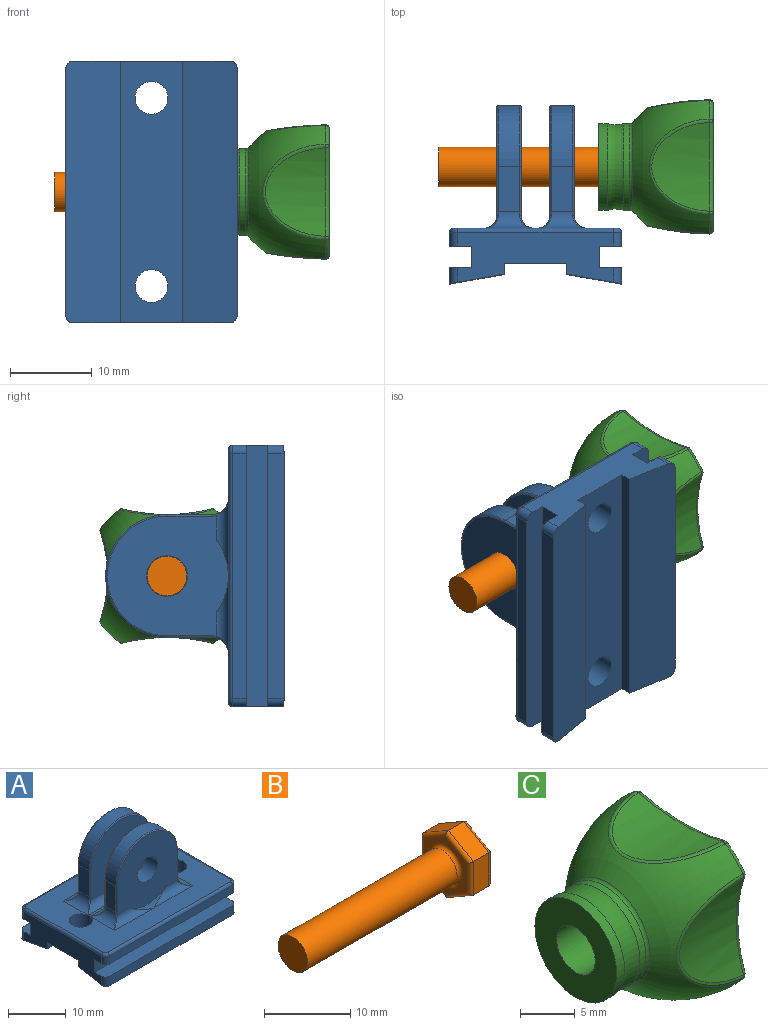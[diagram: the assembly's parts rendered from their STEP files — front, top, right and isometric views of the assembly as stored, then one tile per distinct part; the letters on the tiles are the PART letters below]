
ASSEMBLY  parts=3 mates=4
PART A: 92 faces, bbox 32.2x21.2x22.5 mm
  f0: cylinder r=1.5mm len=9.5mm, axis (1,0,0), area 13.6mm2, adj f11,f23,f50,f75
  f1: cylinder r=1.5mm len=9.5mm, axis (1,0,0), area 13.6mm2, adj f11,f23,f44,f75
  f2: cylinder r=1.5mm len=9.5mm, axis (1,0,0), area 13.6mm2, adj f19,f23,f57,f74
  f3: cylinder r=1.5mm len=9.5mm, axis (1,0,0), area 13.6mm2, adj f19,f23,f51,f74
  f4: cylinder r=1.5mm len=9.5mm, axis (-1,0,0), area 13.6mm2, adj f13,f23,f65,f73
  f5: cylinder r=1.5mm len=9.5mm, axis (-1,0,0), area 13.6mm2, adj f13,f23,f71,f73
  f6: cylinder r=1.5mm len=9.5mm, axis (-1,0,0), area 13.6mm2, adj f18,f23,f58,f72
  f7: cylinder r=1.5mm len=9.5mm, axis (-1,0,0), area 13.6mm2, adj f18,f23,f64,f72
  f8: plane 5.5x2.6mm, normal (-1,0,0), area 14.3mm2, adj f9,f39,f46,f67
  f9: cylinder r=7.5mm len=15mm, axis (0,1,0), area 61.3mm2, adj f8,f10,f47,f68
  f10: plane 5.5x2.6mm, normal (1,0,0), area 14.3mm2, adj f9,f38,f48,f69
  f11: plane 14.8x14.72mm, normal (0,1,0), area 160.9mm2, adj f0,f1,f12,f45,f46,f47,f48,f49
  f12: cylinder r=2.5mm len=5mm, axis (0,1,0), area 47.1mm2, adj f11,f13
  f13: plane 14.8x14.72mm, normal (0,-1,0), area 160.9mm2, adj f4,f5,f12,f66,f67,f68,f69,f70
  f14: plane 5.5x2.6mm, normal (1,0,0), area 14.3mm2, adj f15,f41,f55,f62
  f15: cylinder r=7.5mm len=15mm, axis (0,1,0), area 61.3mm2, adj f14,f16,f54,f61
  f16: plane 5.5x2.6mm, normal (-1,0,0), area 14.3mm2, adj f15,f40,f53,f60
  f17: cylinder r=2.5mm len=5mm, axis (0,1,0), area 47.1mm2, adj f18,f19
  f18: plane 14.8x14.72mm, normal (0,-1,0), area 160.9mm2, adj f6,f7,f17,f59,f60,f61,f62,f63
  f19: plane 14.8x14.72mm, normal (0,1,0), area 160.9mm2, adj f2,f3,f17,f52,f53,f54,f55,f56
  f20: plane 32x2.6mm, normal (0,1,0), area 83.2mm2, adj f21,f35,f36,f37
  f21: plane 32x2.7mm, normal (0,0,-1), area 86mm2, adj f20,f22,f36,f37,f79,f83
  f22: plane 30x1.7mm, normal (0,1,0), area 51mm2, adj f21,f79,f83,f88
  f23: plane 31x20mm, normal (0,0,1), area 366.7mm2, adj f0,f1,f2,f3,f4,f5,f6,f7
  f24: plane 30x1.7mm, normal (0,-1,0), area 51mm2, adj f25,f78,f82,f87
  f25: plane 32x2.7mm, normal (0,0,-1), area 86mm2, adj f24,f26,f36,f37,f78,f82
  f26: plane 32x2.6mm, normal (0,-1,0), area 83.2mm2, adj f25,f27,f36,f37
  f27: plane 32x2.7mm, normal (0,0,1), area 86mm2, adj f26,f28,f36,f37,f77,f81
  f28: plane 30x2mm, normal (0,-1,0), area 60mm2, adj f27,f29,f77,f81
  f29: plane 32.07x6.77mm, normal (0,0.17,-0.98), area 217.3mm2, adj f28,f30,f36,f37,f77,f81
  f30: plane 32x1.32mm, normal (0,1,0), area 42.1mm2, adj f29,f31,f36,f37
  f31: plane 32x7.6mm, normal (0,0,-1), area 218.1mm2, adj f30,f32,f36,f37,f42,f43
  f32: plane 32x1.32mm, normal (0,-1,0), area 42.1mm2, adj f31,f33,f36,f37
  f33: plane 32.07x6.77mm, normal (0,-0.17,-0.98), area 217.3mm2, adj f32,f34,f36,f37,f76,f80
  f34: plane 30x2mm, normal (0,1,0), area 60mm2, adj f33,f35,f76,f80
  f35: plane 32x2.7mm, normal (0,0,1), area 86mm2, adj f20,f34,f36,f37,f76,f80
  f36: plane 19x6.12mm, normal (1,0,0), area 84.1mm2, adj f20,f21,f25,f26,f27,f29,f30,f31
  f37: plane 19x6.12mm, normal (-1,0,0), area 84.1mm2, adj f20,f21,f25,f26,f27,f29,f30,f31
  f38: cylinder r=2mm len=6mm, axis (0,-1,0), area 11.6mm2, adj f10,f23,f49,f50,f70,f71
  f39: cylinder r=2mm len=6mm, axis (0,1,0), area 11.6mm2, adj f8,f23,f44,f45,f65,f66
  f40: cylinder r=2mm len=6mm, axis (0,1,0), area 11.6mm2, adj f16,f23,f51,f52,f58,f59
  f41: cylinder r=2mm len=6mm, axis (0,-1,0), area 11.6mm2, adj f14,f23,f56,f57,f63,f64
  f42: cylinder r=2mm len=4.3mm, axis (0,0,1), area 54mm2, adj f23,f31
  f43: cylinder r=2mm len=4.3mm, axis (0,0,1), area 54mm2, adj f23,f31
  f44: bspline ~2.19x1.83mm, area 0.5mm2, adj f1,f39,f45
  f45: torus R=2.2mm, axis (0,-1,0), area 0.1mm2, adj f11,f39,f44,f46
  f46: cylinder r=0.2mm len=5.5mm, axis (0,0,-1), area 1.7mm2, adj f8,f11,f45,f47
  f47: torus R=7.3mm, axis (0,-1,0), area 7.3mm2, adj f9,f11,f46,f48
  f48: cylinder r=0.2mm len=5.5mm, axis (0,0,1), area 1.7mm2, adj f10,f11,f47,f49
  f49: torus R=2.2mm, axis (0,-1,0), area 0.1mm2, adj f11,f38,f48,f50
  f50: bspline ~2.19x1.83mm, area 0.5mm2, adj f0,f38,f49
  f51: bspline ~2.19x1.83mm, area 0.5mm2, adj f3,f40,f52
  f52: torus R=2.2mm, axis (0,-1,0), area 0.1mm2, adj f19,f40,f51,f53
  f53: cylinder r=0.2mm len=5.5mm, axis (0,0,-1), area 1.7mm2, adj f16,f19,f52,f54
  f54: torus R=7.3mm, axis (0,-1,0), area 7.3mm2, adj f15,f19,f53,f55
  f55: cylinder r=0.2mm len=5.5mm, axis (0,0,1), area 1.7mm2, adj f14,f19,f54,f56
  f56: torus R=2.2mm, axis (0,-1,0), area 0.1mm2, adj f19,f41,f55,f57
  f57: bspline ~2.19x1.83mm, area 0.5mm2, adj f2,f41,f56
  f58: bspline ~2.19x1.83mm, area 0.5mm2, adj f6,f40,f59
  f59: torus R=2.2mm, axis (0,-1,0), area 0.1mm2, adj f18,f40,f58,f60
  f60: cylinder r=0.2mm len=5.5mm, axis (0,0,1), area 1.7mm2, adj f16,f18,f59,f61
  f61: torus R=7.3mm, axis (0,-1,0), area 7.3mm2, adj f15,f18,f60,f62
  f62: cylinder r=0.2mm len=5.5mm, axis (0,0,-1), area 1.7mm2, adj f14,f18,f61,f63
  f63: torus R=2.2mm, axis (0,-1,0), area 0.1mm2, adj f18,f41,f62,f64
  f64: bspline ~2.19x1.83mm, area 0.5mm2, adj f7,f41,f63
  f65: bspline ~2.19x1.83mm, area 0.5mm2, adj f4,f39,f66
  f66: torus R=2.2mm, axis (0,-1,0), area 0.1mm2, adj f13,f39,f65,f67
  f67: cylinder r=0.2mm len=5.5mm, axis (0,0,1), area 1.7mm2, adj f8,f13,f66,f68
  f68: torus R=7.3mm, axis (0,-1,0), area 7.3mm2, adj f9,f13,f67,f69
  f69: cylinder r=0.2mm len=5.5mm, axis (0,0,-1), area 1.7mm2, adj f10,f13,f68,f70
  f70: torus R=2.2mm, axis (0,-1,0), area 0.1mm2, adj f13,f38,f69,f71
  f71: bspline ~2.19x1.83mm, area 0.5mm2, adj f5,f38,f70
  f72: cylinder r=7.5mm len=9mm, axis (0,1,0), area 5.6mm2, adj f6,f7,f18
  f73: cylinder r=7.5mm len=9mm, axis (0,-1,0), area 5.6mm2, adj f4,f5,f13
  f74: cylinder r=7.5mm len=9mm, axis (0,-1,0), area 5.6mm2, adj f2,f3,f19
  f75: cylinder r=7.5mm len=9mm, axis (0,-1,0), area 5.6mm2, adj f0,f1,f11
  f76: cylinder r=1mm len=2mm, axis (0,0,1), area 3mm2, adj f33,f34,f35,f37
  f77: cylinder r=1mm len=2mm, axis (0,0,-1), area 3mm2, adj f27,f28,f29,f37
  f78: cylinder r=1mm len=1.7mm, axis (0,0,-1), area 2.7mm2, adj f24,f25,f37,f85
  f79: cylinder r=1mm len=1.7mm, axis (0,0,1), area 2.7mm2, adj f21,f22,f37,f86
  f80: cylinder r=1mm len=2mm, axis (0,0,-1), area 3mm2, adj f33,f34,f35,f36
  f81: cylinder r=1mm len=2mm, axis (0,0,1), area 3mm2, adj f27,f28,f29,f36
  f82: cylinder r=1mm len=1.7mm, axis (0,0,1), area 2.7mm2, adj f24,f25,f36,f89
  f83: cylinder r=1mm len=1.7mm, axis (0,0,-1), area 2.7mm2, adj f21,f22,f36,f90
  f84: cylinder r=0.5mm len=19mm, axis (0,-1,0), area 14.9mm2, adj f23,f37,f85,f86
  f85: torus R=0.5mm, axis (0,0,1), area 1mm2, adj f23,f78,f84,f87
  f86: torus R=0.5mm, axis (0,0,1), area 1mm2, adj f23,f79,f84,f88
  f87: cylinder r=0.5mm len=30mm, axis (1,0,0), area 23.6mm2, adj f23,f24,f85,f89
  f88: cylinder r=0.5mm len=30mm, axis (-1,0,0), area 23.6mm2, adj f22,f23,f86,f90
  f89: torus R=0.5mm, axis (0,0,1), area 1mm2, adj f23,f82,f87,f91
  f90: torus R=0.5mm, axis (0,0,1), area 1mm2, adj f23,f83,f88,f91
  f91: cylinder r=0.5mm len=19mm, axis (0,1,0), area 14.9mm2, adj f23,f36,f89,f90
PART B: 23 faces, bbox 28.5x8.2x9.5 mm
  f0: cylinder r=2.42mm len=24.5mm, axis (1,0,0), area 371.8mm2, adj f1,f22
  f1: plane 4.83x4.83mm, normal (-1,0,0), area 18.3mm2, adj f0
  f2: plane 4.73x2.5mm, normal (0,1,0), area 11.8mm2, adj f3,f7,f11,f17
  f3: plane 4.1x2.5mm, normal (0,0.5,0.87), area 11.8mm2, adj f2,f4,f10,f16
  f4: plane 4.1x2.5mm, normal (0,-0.5,0.87), area 11.8mm2, adj f3,f5,f12,f18
  f5: plane 4.73x2.5mm, normal (0,-1,0), area 11.8mm2, adj f4,f6,f14,f20
  f6: plane 4.1x2.5mm, normal (0,-0.5,-0.87), area 11.8mm2, adj f5,f7,f15,f21
  f7: plane 4.1x2.5mm, normal (0,0.5,-0.87), area 11.8mm2, adj f2,f6,f13,f19
  f8: plane 8.31x7.2mm, normal (1,0,0), area 44.9mm2, adj f16,f17,f18,f19,f20,f21
  f9: plane 8.31x7.2mm, normal (-1,0,0), area 18.2mm2, adj f10,f11,f12,f13,f14,f15,f22
  f10: cylinder r=0.5mm len=4.35mm, axis (0,-0.87,0.5), area 3.6mm2, adj f3,f9,f11,f12
  f11: cylinder r=0.5mm len=4.73mm, axis (0,0,1), area 3.6mm2, adj f2,f9,f10,f13
  f12: cylinder r=0.5mm len=4.35mm, axis (0,-0.87,-0.5), area 3.6mm2, adj f4,f9,f10,f14
  f13: cylinder r=0.5mm len=4.35mm, axis (0,0.87,0.5), area 3.6mm2, adj f7,f9,f11,f15
  f14: cylinder r=0.5mm len=4.73mm, axis (0,0,-1), area 3.6mm2, adj f5,f9,f12,f15
  f15: cylinder r=0.5mm len=4.35mm, axis (0,0.87,-0.5), area 3.6mm2, adj f6,f9,f13,f14
  f16: cylinder r=0.5mm len=4.35mm, axis (0,0.87,-0.5), area 3.6mm2, adj f3,f8,f17,f18
  f17: cylinder r=0.5mm len=4.73mm, axis (0,0,-1), area 3.6mm2, adj f2,f8,f16,f19
  f18: cylinder r=0.5mm len=4.35mm, axis (0,0.87,0.5), area 3.6mm2, adj f4,f8,f16,f20
  f19: cylinder r=0.5mm len=4.35mm, axis (0,-0.87,-0.5), area 3.6mm2, adj f7,f8,f17,f21
  f20: cylinder r=0.5mm len=4.73mm, axis (0,0,1), area 3.6mm2, adj f5,f8,f18,f21
  f21: cylinder r=0.5mm len=4.35mm, axis (0,-0.87,0.5), area 3.6mm2, adj f6,f8,f19,f20
  f22: torus R=2.92mm, axis (1,0,0), area 12.8mm2, adj f0,f9
PART C: 45 faces, bbox 15.2x20x20 mm
  f0: cylinder r=2.5mm len=5.4mm, axis (1,0,0), area 84.8mm2, adj f3,f11
  f1: revolved ~19.99x19.99mm, area 260.8mm2, adj f18,f19,f20,f21,f22,f23,f24,f25
  f2: plane 15.41x15.38mm, normal (1,0,0), area 95.7mm2, adj f19,f20,f23,f24,f28,f31,f34,f37
  f3: plane 10.6x10.6mm, normal (-1,0,0), area 68.6mm2, adj f0,f4
  f4: cylinder r=5.3mm len=10.6mm, axis (1,0,0), area 33.3mm2, adj f3,f5
  f5: torus R=8.13mm, axis (1,0,0), area 66.4mm2, adj f4,f6
  f6: cylinder r=5.3mm len=10.6mm, axis (1,0,0), area 25.5mm2, adj f5,f26
  f7: cylinder r=16.47mm len=10.81mm, axis (1,0,0), area 62.3mm2, adj f22,f28
  f8: cylinder r=16.47mm len=10.81mm, axis (1,0,0), area 62.3mm2, adj f21,f31
  f9: cylinder r=21.67mm len=10.85mm, axis (1,0,0), area 59.4mm2, adj f18,f34
  f10: cylinder r=21.67mm len=10.85mm, axis (1,0,0), area 59.4mm2, adj f25,f37
  f11: plane 9.7x8.4mm, normal (1,0,0), area 41.5mm2, adj f0,f12,f13,f14,f15,f16,f17
  f12: plane 7.65x5.31mm, normal (0.05,1,0), area 38.9mm2, adj f11,f13,f17,f43
  f13: plane 7.65x4.6mm, normal (0.05,0.5,0.86), area 38.9mm2, adj f11,f12,f14,f44
  f14: plane 7.65x4.6mm, normal (0.05,-0.5,0.86), area 38.9mm2, adj f11,f13,f15,f42
  f15: plane 7.65x5.31mm, normal (0.05,-1,0), area 38.9mm2, adj f11,f14,f16,f40
  f16: plane 7.65x4.6mm, normal (0.05,-0.5,-0.86), area 38.9mm2, adj f11,f15,f17,f39
  f17: plane 7.65x4.6mm, normal (0.05,0.5,-0.86), area 38.9mm2, adj f11,f12,f16,f41
  f18: bspline ~11.7x8.21mm, area 7.8mm2, adj f1,f9,f33,f35
  f19: torus R=9.49mm, axis (-1,0,0), area 2.5mm2, adj f1,f2,f32,f35
  f20: torus R=9.49mm, axis (-1,0,0), area 2.5mm2, adj f1,f2,f29,f33
  f21: bspline ~11.75x8.97mm, area 8.7mm2, adj f1,f8,f30,f32
  f22: bspline ~11.75x8.97mm, area 8.7mm2, adj f1,f7,f27,f29
  f23: torus R=9.49mm, axis (-1,0,0), area 2.5mm2, adj f1,f2,f30,f38
  f24: torus R=9.49mm, axis (-1,0,0), area 2.5mm2, adj f1,f2,f27,f36
  f25: bspline ~11.71x8.9mm, area 7.8mm2, adj f1,f10,f36,f38
  f26: torus R=5.8mm, axis (1,0,0), area 14.7mm2, adj f1,f6
  f27: sphere r=0.5mm, area 0.2mm2, adj f22,f24,f28
  f28: torus R=16.97mm, axis (-1,0,0), area 8.7mm2, adj f2,f7,f27,f29
  f29: sphere r=0.5mm, area 0.2mm2, adj f20,f22,f28
  f30: sphere r=0.5mm, area 0.2mm2, adj f21,f23,f31
  f31: torus R=16.97mm, axis (-1,0,0), area 8.7mm2, adj f2,f8,f30,f32
  f32: sphere r=0.5mm, area 0.2mm2, adj f19,f21,f31
  f33: sphere r=0.5mm, area 0.2mm2, adj f18,f20,f34
  f34: torus R=22.17mm, axis (-1,0,0), area 8.7mm2, adj f2,f9,f33,f35
  f35: sphere r=0.5mm, area 0.2mm2, adj f18,f19,f34
  f36: sphere r=0.5mm, area 0.2mm2, adj f24,f25,f37
  f37: torus R=22.17mm, axis (-1,0,0), area 8.7mm2, adj f2,f10,f36,f38
  f38: sphere r=0.5mm, area 0.2mm2, adj f23,f25,f37
  f39: cylinder r=1mm len=6.1mm, axis (0,-0.87,0.5), area 8.7mm2, adj f2,f16,f40,f41
  f40: cylinder r=1mm len=6.47mm, axis (0,0,1), area 8.7mm2, adj f2,f15,f39,f42
  f41: cylinder r=1mm len=6.1mm, axis (0,-0.87,-0.5), area 8.7mm2, adj f2,f17,f39,f43
  f42: cylinder r=1mm len=6.1mm, axis (0,0.87,0.5), area 8.7mm2, adj f2,f14,f40,f44
  f43: cylinder r=1mm len=6.47mm, axis (0,0,-1), area 8.7mm2, adj f2,f12,f41,f44
  f44: cylinder r=1mm len=6.1mm, axis (0,0.87,-0.5), area 8.7mm2, adj f2,f13,f42,f43
PLACE A rot(axis=(-0.58,-0.58,-0.58),120deg) t=(-9.87,-7.1,0)mm
PLACE B t=(-20.65,0.4,0)mm
PLACE C t=(-9.65,0.4,0)mm
MATE cylindrical B.f0 <-> A.f9  axis (1,0,0) through (-9.47,0.4,0)mm
MATE cylindrical C.f0 <-> B.f0  axis (1,0,0) through (0.58,0.4,0)mm
MATE planar A.f11 <-> C.f0  axis (1,0,0) through (-5.12,0,0)mm
MATE planar C.f11 <-> B.f9  axis (1,0,0) through (3.28,4.6,0)mm
